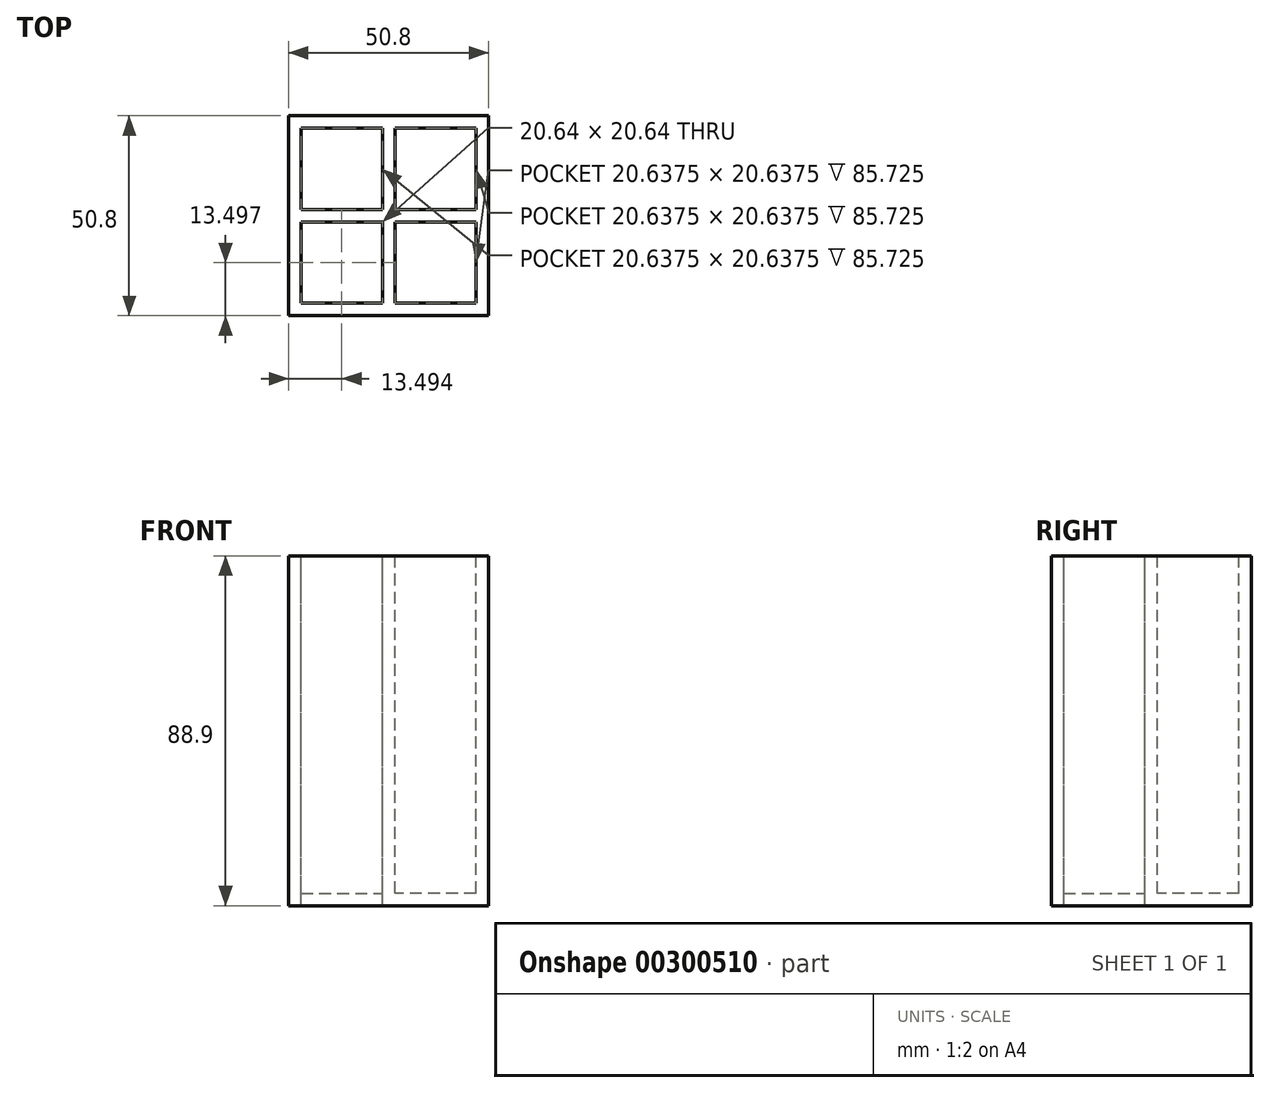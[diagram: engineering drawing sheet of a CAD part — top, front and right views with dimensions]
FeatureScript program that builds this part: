
annotation { "Feature Type Name" : "Feature", "Feature Type Description" : "" }
export const myFeature = defineFeature(function(context is Context, id is Id, definition is map)
    precondition{}
    {
        {
            var Q0;
            Q0=qCreatedBy(makeId("Top.planeOp"),FACE);
            var sketch = newSketch(context, id + "F0", { "sketchPlane" : qUnion([Q0])});
            skLineSegment(sketch, "E0.bottom", {"start": v(-25.4, 25.36) * mm, "end": v(25.4, 25.36) * mm});
            skLineSegment(sketch, "E0.top", {"start": v(-25.4, -25.44) * mm, "end": v(25.4, -25.44) * mm});
            skLineSegment(sketch, "E0.left", {"start": v(-25.4, 25.36) * mm, "end": v(-25.4, -25.44) * mm});
            skLineSegment(sketch, "E0.right", {"start": v(25.4, 25.36) * mm, "end": v(25.4, -25.44) * mm});
            skLineSegment(sketch, "E1.bottom", {"start": v(-22.23, -22.26) * mm, "end": v(-1.59, -22.26) * mm});
            skLineSegment(sketch, "E1.top", {"start": v(-22.23, -1.62) * mm, "end": v(-1.59, -1.62) * mm});
            skLineSegment(sketch, "E1.left", {"start": v(-22.23, -22.26) * mm, "end": v(-22.23, -1.62) * mm});
            skLineSegment(sketch, "E1.right", {"start": v(-1.59, -22.26) * mm, "end": v(-1.59, -1.62) * mm});
            skLineSegment(sketch, "E2.bottom", {"start": v(22.23, -22.26) * mm, "end": v(1.59, -22.26) * mm});
            skLineSegment(sketch, "E2.top", {"start": v(22.23, -1.62) * mm, "end": v(1.59, -1.62) * mm});
            skLineSegment(sketch, "E2.left", {"start": v(22.23, -22.26) * mm, "end": v(22.23, -1.62) * mm});
            skLineSegment(sketch, "E2.right", {"start": v(1.59, -22.26) * mm, "end": v(1.59, -1.62) * mm});
            skLineSegment(sketch, "E3.bottom", {"start": v(-22.23, 22.19) * mm, "end": v(-1.59, 22.19) * mm});
            skLineSegment(sketch, "E3.top", {"start": v(-22.23, 1.55) * mm, "end": v(-1.59, 1.55) * mm});
            skLineSegment(sketch, "E3.left", {"start": v(-22.23, 22.19) * mm, "end": v(-22.23, 1.55) * mm});
            skLineSegment(sketch, "E3.right", {"start": v(-1.59, 22.19) * mm, "end": v(-1.59, 1.55) * mm});
            skLineSegment(sketch, "E4.bottom", {"start": v(22.23, 22.19) * mm, "end": v(1.59, 22.19) * mm});
            skLineSegment(sketch, "E4.top", {"start": v(22.23, 1.55) * mm, "end": v(1.59, 1.55) * mm});
            skLineSegment(sketch, "E4.left", {"start": v(22.23, 22.19) * mm, "end": v(22.23, 1.55) * mm});
            skLineSegment(sketch, "E4.right", {"start": v(1.59, 22.19) * mm, "end": v(1.59, 1.55) * mm});
            skSolve(sketch);
        }
        {
            var Q0;
            Q0 = qSketchRegion(id + "F0", true);
            extrude(context, id + "F1", {"entities" : qUnion([Q0]), "oppositeDirection" : true, "depth" : 88.9 * mm});
        }
        {
            var Q0;
            Q0=makeQuery(id+"F1.opExtrude","CAP_FACE",FACE,{"disambiguationData":[OSD([sQuery(id+"F0.wireOp",EDGE,"E0.bottom"),sQuery(id+"F0.wireOp",EDGE,"E0.top"),sQuery(id+"F0.wireOp",EDGE,"E0.left"),sQuery(id+"F0.wireOp",EDGE,"E0.right"),sQuery(id+"F0.wireOp",EDGE,"E1.bottom"),sQuery(id+"F0.wireOp",EDGE,"E1.top"),sQuery(id+"F0.wireOp",EDGE,"E1.left"),sQuery(id+"F0.wireOp",EDGE,"E1.right"),sQuery(id+"F0.wireOp",EDGE,"E2.bottom"),sQuery(id+"F0.wireOp",EDGE,"E2.top"),sQuery(id+"F0.wireOp",EDGE,"E2.left"),sQuery(id+"F0.wireOp",EDGE,"E2.right"),sQuery(id+"F0.wireOp",EDGE,"E3.bottom"),sQuery(id+"F0.wireOp",EDGE,"E3.top"),sQuery(id+"F0.wireOp",EDGE,"E3.left"),sQuery(id+"F0.wireOp",EDGE,"E3.right"),sQuery(id+"F0.wireOp",EDGE,"E4.bottom"),sQuery(id+"F0.wireOp",EDGE,"E4.top"),sQuery(id+"F0.wireOp",EDGE,"E4.left"),sQuery(id+"F0.wireOp",EDGE,"E4.right")])],"isStart":false});
            var sketch = newSketch(context, id + "F2", { "sketchPlane" : qUnion([Q0])});
            skLineSegment(sketch, "E5.bottom", {"start": v(-22.23, 22.26) * mm, "end": v(-1.59, 22.26) * mm});
            skLineSegment(sketch, "E5.top", {"start": v(-22.23, 1.62) * mm, "end": v(-1.59, 1.62) * mm});
            skLineSegment(sketch, "E5.left", {"start": v(-22.23, 22.26) * mm, "end": v(-22.23, 1.62) * mm});
            skLineSegment(sketch, "E5.right", {"start": v(-1.59, 22.26) * mm, "end": v(-1.59, 1.62) * mm});
            skLineSegment(sketch, "E6.bottom", {"start": v(1.59, 22.26) * mm, "end": v(22.23, 22.26) * mm});
            skLineSegment(sketch, "E6.top", {"start": v(1.59, 1.62) * mm, "end": v(22.23, 1.62) * mm});
            skLineSegment(sketch, "E6.left", {"start": v(1.59, 22.26) * mm, "end": v(1.59, 1.62) * mm});
            skLineSegment(sketch, "E6.right", {"start": v(22.23, 22.26) * mm, "end": v(22.23, 1.62) * mm});
            skLineSegment(sketch, "E7.bottom", {"start": v(1.59, -1.55) * mm, "end": v(22.23, -1.55) * mm});
            skLineSegment(sketch, "E7.top", {"start": v(1.59, -22.19) * mm, "end": v(22.23, -22.19) * mm});
            skLineSegment(sketch, "E7.left", {"start": v(1.59, -1.55) * mm, "end": v(1.59, -22.19) * mm});
            skLineSegment(sketch, "E7.right", {"start": v(22.23, -1.55) * mm, "end": v(22.23, -22.19) * mm});
            skLineSegment(sketch, "E8.bottom", {"start": v(-22.23, -1.55) * mm, "end": v(-1.59, -1.55) * mm});
            skLineSegment(sketch, "E8.top", {"start": v(-22.23, -22.19) * mm, "end": v(-1.59, -22.19) * mm});
            skLineSegment(sketch, "E8.left", {"start": v(-22.23, -1.55) * mm, "end": v(-22.23, -22.19) * mm});
            skLineSegment(sketch, "E8.right", {"start": v(-1.59, -1.55) * mm, "end": v(-1.59, -22.19) * mm});
            skLineSegment(sketch, "E9.bottom", {"start": v(-1.59, 1.62) * mm, "end": v(-22.23, 1.62) * mm});
            skLineSegment(sketch, "E9.top", {"start": v(-1.59, 22.26) * mm, "end": v(-22.23, 22.26) * mm});
            skLineSegment(sketch, "E9.left", {"start": v(-1.59, 1.62) * mm, "end": v(-1.59, 22.26) * mm});
            skLineSegment(sketch, "E9.right", {"start": v(-22.23, 1.62) * mm, "end": v(-22.23, 22.26) * mm});
            skSolve(sketch);
        }
        {
            var Q0;
            Q0=makeQuery(id+"F2.imprint","IMPRINT",FACE,{"disambiguationData":[TD([[makeQuery(id+"F2.imprint","IMPRINT",EDGE,{"derivedFrom":sQuery(id+"F2.wireOp",EDGE,"E9.bottom")}),1.0]])]});
            var Q1;
            Q1=makeQuery(id+"F2.imprint","IMPRINT",FACE,{"disambiguationData":[TD([[makeQuery(id+"F2.imprint","IMPRINT",EDGE,{"derivedFrom":sQuery(id+"F2.wireOp",EDGE,"E6.bottom")}),1.0]])]});
            var Q2;
            Q2=makeQuery(id+"F2.imprint","IMPRINT",FACE,{"disambiguationData":[TD([[makeQuery(id+"F2.imprint","IMPRINT",EDGE,{"derivedFrom":sQuery(id+"F2.wireOp",EDGE,"E7.bottom")}),1.0]])]});
            var Q3;
            Q3=makeQuery(id+"F2.imprint","IMPRINT",FACE,{"disambiguationData":[TD([[makeQuery(id+"F2.imprint","IMPRINT",EDGE,{"derivedFrom":sQuery(id+"F2.wireOp",EDGE,"E8.bottom")}),-1.0]])]});
            extrude(context, id + "F3", {"entities" : qUnion([Q0, Q1, Q2, Q3]), "operationType" : NewBodyOperationType.ADD, "oppositeDirection" : true, "depth" : 3.17 * mm});
        }
    });
